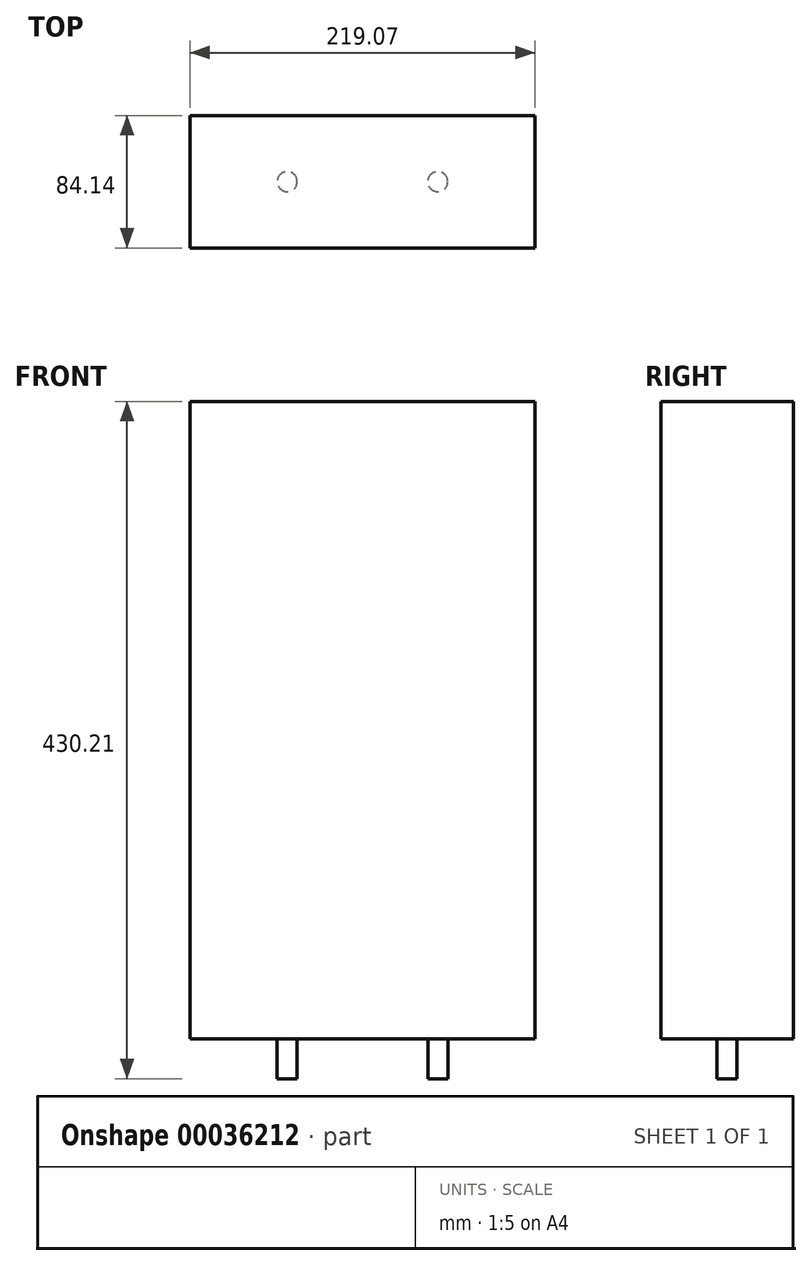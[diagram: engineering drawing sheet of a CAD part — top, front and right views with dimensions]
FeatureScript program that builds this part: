
annotation { "Feature Type Name" : "Feature", "Feature Type Description" : "" }
export const myFeature = defineFeature(function(context is Context, id is Id, definition is map)
    precondition{}
    {
        {
            var Q0;
            Q0=qCreatedBy(makeId("Front.planeOp"),FACE);
            var sketch = newSketch(context, id + "F0", { "sketchPlane" : qUnion([Q0])});
            skLineSegment(sketch, "E0.bottom", {"start": v(0, 0) * mm, "end": v(219.08, 0) * mm});
            skLineSegment(sketch, "E0.top", {"start": v(0, 404.81) * mm, "end": v(219.07, 404.81) * mm});
            skLineSegment(sketch, "E0.left", {"start": v(0, 0) * mm, "end": v(0, 404.81) * mm});
            skLineSegment(sketch, "E0.right", {"start": v(219.08, 0) * mm, "end": v(219.08, 404.81) * mm});
            skSolve(sketch);
        }
        {
            var Q0;
            Q0 = qSketchRegion(id + "F0", true);
            extrude(context, id + "F1", {"entities" : qUnion([Q0]), "depth" : 84.14 * mm, "symmetric" : true});
        }
        {
            var Q0;
            Q0=qCreatedBy(makeId("Front.planeOp"),FACE);
            var sketch = newSketch(context, id + "F2", { "sketchPlane" : qUnion([Q0])});
            skLineSegment(sketch, "E1.bottom", {"start": v(55.37, 0) * mm, "end": v(61.72, 0) * mm});
            skLineSegment(sketch, "E1.top", {"start": v(55.37, -25.4) * mm, "end": v(61.72, -25.4) * mm});
            skLineSegment(sketch, "E1.left", {"start": v(55.37, 0) * mm, "end": v(55.37, -25.4) * mm});
            skLineSegment(sketch, "E1.right", {"start": v(61.72, 0) * mm, "end": v(61.72, -25.4) * mm});
            skLineSegment(sketch, "E2.bottom", {"start": v(157.35, 0) * mm, "end": v(163.7, 0) * mm});
            skLineSegment(sketch, "E2.top", {"start": v(157.35, -25.4) * mm, "end": v(163.7, -25.4) * mm});
            skLineSegment(sketch, "E2.left", {"start": v(157.35, 0) * mm, "end": v(157.35, -25.4) * mm});
            skLineSegment(sketch, "E2.right", {"start": v(163.7, 0) * mm, "end": v(163.7, -25.4) * mm});
            skLineSegment(sketch, "E3", {"start": v(61.72, 52.1) * mm, "end": v(61.72, -133.53) * mm, "construction": true});
            skLineSegment(sketch, "E4", {"start": v(157.35, 50.72) * mm, "end": v(157.35, -144.17) * mm, "construction": true});
            skSolve(sketch);
        }
        {
            var Q0;
            Q0=makeQuery(id+"F2.imprint","IMPRINT",FACE,{"disambiguationData":[TD([[makeQuery(id+"F2.imprint","IMPRINT",EDGE,{"derivedFrom":sQuery(id+"F2.wireOp",EDGE,"E1.bottom")}),-1.0]])]});
            var Q1;
            Q1=sQuery(id+"F2.wireOp",EDGE,"E3");
            revolve(context, id + "F3", {"operationType" : NewBodyOperationType.ADD, "entities" : qUnion([Q0]), "axis" : qUnion([Q1]), "revolveType" : RevolveType.FULL});
        }
        {
            var Q0;
            Q0=makeQuery(id+"F2.imprint","IMPRINT",FACE,{"disambiguationData":[TD([[makeQuery(id+"F2.imprint","IMPRINT",EDGE,{"derivedFrom":sQuery(id+"F2.wireOp",EDGE,"E2.bottom")}),-1.0]])]});
            var Q1;
            Q1=sQuery(id+"F2.wireOp",EDGE,"E4");
            revolve(context, id + "F4", {"operationType" : NewBodyOperationType.ADD, "entities" : qUnion([Q0]), "axis" : qUnion([Q1]), "revolveType" : RevolveType.FULL});
        }
    });
